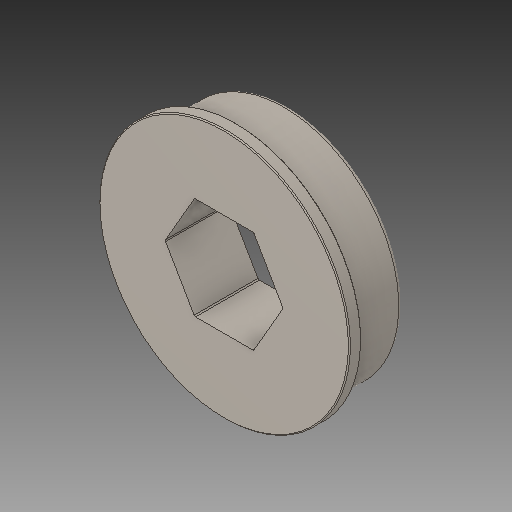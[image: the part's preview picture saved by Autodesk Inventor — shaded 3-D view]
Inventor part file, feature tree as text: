
AUTODESK INVENTOR PART (.ipt)
format: ipt  version: 2018.2 (Build 222227000, 227)  size: 146,432 bytes
history: native  units: in
note: dims shown in document units (in); Inventor stores cm internally (conversion verified against a paired STEP export)
features: fillet x1
ambient origin geometry x8: Origin, YZ Plane, XZ Plane, XY Plane, X Axis, Y Axis, Z Axis, Center Point
bodies: Solid1 (feature_tree)
feature tree (1):
  fillet  "Fillet2"  [1 undecoded]
note: 1 required parameter value undecoded (feature->parameter linkage not recoverable at this tier; creation-order binding heuristic only, values carry confidence <= 0.55)
